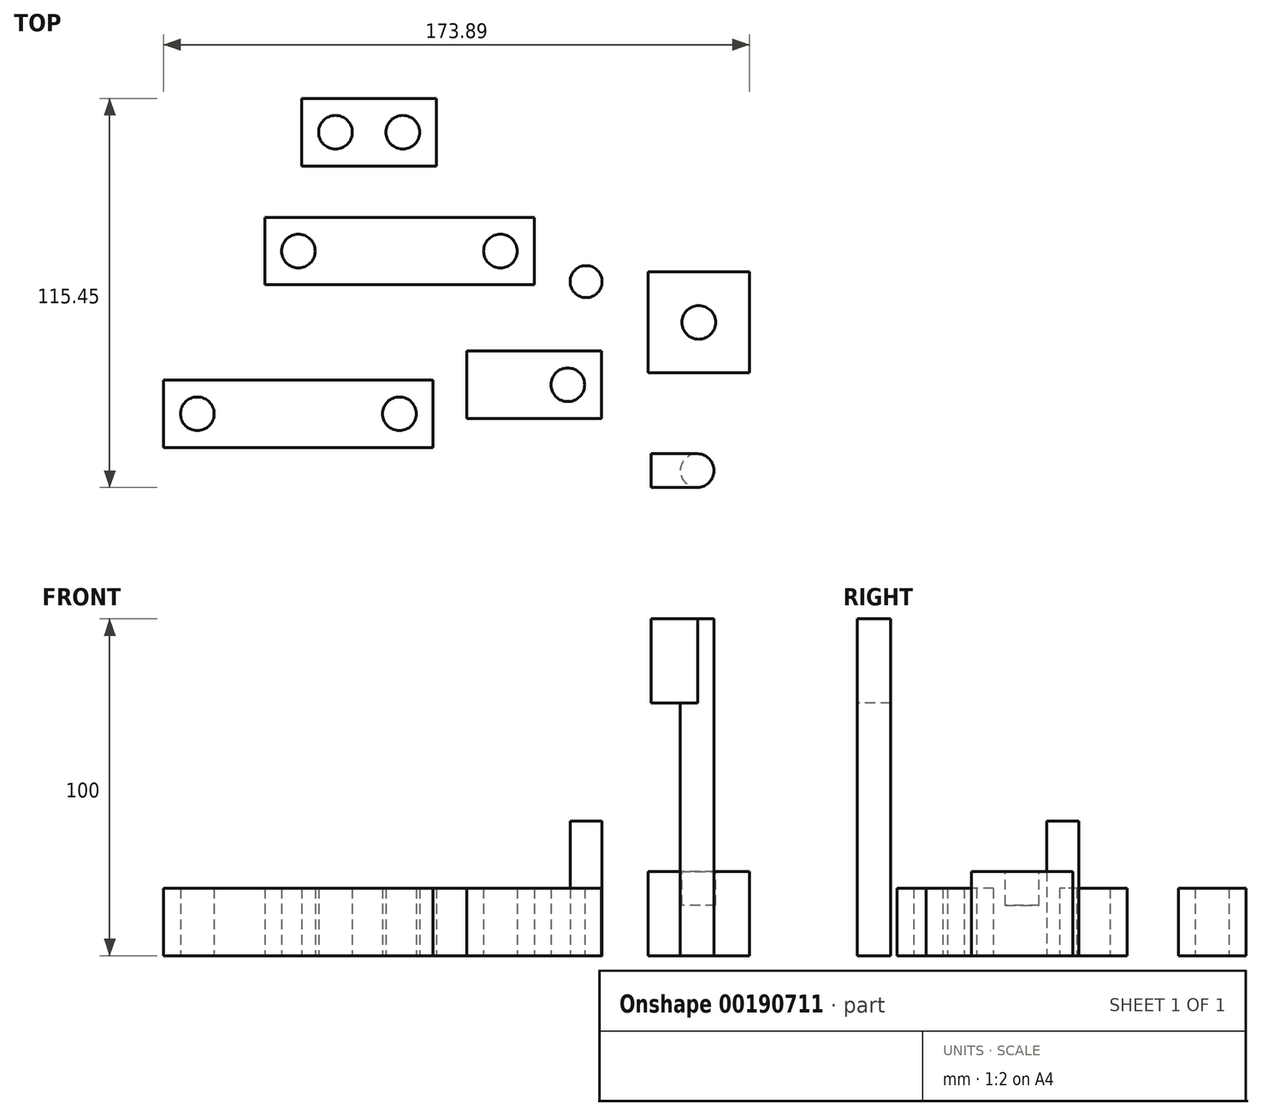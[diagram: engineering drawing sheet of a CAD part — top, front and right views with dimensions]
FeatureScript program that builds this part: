
annotation { "Feature Type Name" : "Feature", "Feature Type Description" : "" }
export const myFeature = defineFeature(function(context is Context, id is Id, definition is map)
    precondition{}
    {
        {
            var Q0;
            Q0=qCreatedBy(makeId("Top.planeOp"),FACE);
            var sketch = newSketch(context, id + "F0", { "sketchPlane" : qUnion([Q0])});
            skLineSegment(sketch, "E0.bottom", {"start": v(-30, 10) * mm, "end": v(10, 10) * mm});
            skLineSegment(sketch, "E0.top", {"start": v(-30, -10) * mm, "end": v(10, -10) * mm});
            skLineSegment(sketch, "E0.left", {"start": v(-30, 10) * mm, "end": v(-30, -10) * mm});
            skLineSegment(sketch, "E0.right", {"start": v(10, 10) * mm, "end": v(10, -10) * mm});
            skCircle(sketch, "E1", {"center": v(0, 0) * mm, "radius": 5 * mm});
            skSolve(sketch);
        }
        {
            var Q0;
            Q0=makeQuery(id+"F0.imprint","IMPRINT",FACE,{"disambiguationData":[TD([[makeQuery(id+"F0.imprint","IMPRINT",EDGE,{"derivedFrom":sQuery(id+"F0.wireOp",EDGE,"E0.bottom")}),-1.0]])]});
            extrude(context, id + "F1", {"entities" : qUnion([Q0]), "depth" : 20 * mm});
        }
        {
            var Q0;
            Q0=qCreatedBy(makeId("Top.planeOp"),FACE);
            var sketch = newSketch(context, id + "F2", { "sketchPlane" : qUnion([Q0])});
            skLineSegment(sketch, "E2.bottom", {"start": v(23.89, 33.53) * mm, "end": v(53.89, 33.53) * mm});
            skLineSegment(sketch, "E2.top", {"start": v(23.89, 3.53) * mm, "end": v(53.89, 3.53) * mm});
            skLineSegment(sketch, "E2.left", {"start": v(23.89, 33.53) * mm, "end": v(23.89, 3.53) * mm});
            skLineSegment(sketch, "E2.right", {"start": v(53.89, 33.53) * mm, "end": v(53.89, 3.53) * mm});
            skSolve(sketch);
        }
        {
            var Q0;
            Q0 = qSketchRegion(id + "F2", true);
            extrude(context, id + "F3", {"entities" : qUnion([Q0]), "depth" : 25 * mm});
        }
        {
            var Q0;
            Q0=makeQuery(id+"F3.opExtrude","CAP_FACE",FACE,{"disambiguationData":[OSD([sQuery(id+"F2.wireOp",EDGE,"E2.bottom"),sQuery(id+"F2.wireOp",EDGE,"E2.top"),sQuery(id+"F2.wireOp",EDGE,"E2.left"),sQuery(id+"F2.wireOp",EDGE,"E2.right"),sQuery(id+"F2.wireOp",EDGE,"gEPdtIbd-Eig8-yS6G-mVio-MUXTbyyWghyp")])],"isStart":false});
            var sketch = newSketch(context, id + "F4", { "sketchPlane" : qUnion([Q0])});
            skCircle(sketch, "E3", {"center": v(38.89, 18.53) * mm, "radius": 5 * mm});
            skPoint(sketch, "E3.first.point", {"position": v(43.88, 18.4) * mm});
            skPoint(sketch, "E3.second.point", {"position": v(39.58, 13.58) * mm});
            skPoint(sketch, "E3.third.point", {"position": v(34.82, 21.44) * mm});
            skSolve(sketch);
        }
        {
            var Q0;
            Q0 = qSketchRegion(id + "F4", true);
            extrude(context, id + "F5", {"entities" : qUnion([Q0]), "operationType" : NewBodyOperationType.REMOVE, "oppositeDirection" : true, "depth" : 10 * mm});
        }
        {
            var Q0;
            Q0=qCreatedBy(makeId("Top.planeOp"),FACE);
            var sketch = newSketch(context, id + "F6", { "sketchPlane" : qUnion([Q0])});
            skCircle(sketch, "E4", {"center": v(38.41, -25.48) * mm, "radius": 5 * mm});
            skSolve(sketch);
        }
        {
            var Q0;
            Q0 = qSketchRegion(id + "F6", true);
            extrude(context, id + "F7", {"entities" : qUnion([Q0]), "depth" : 100 * mm});
        }
        {
            var Q0;
            Q0=makeQuery(id+"F7.opExtrude","CAP_FACE",FACE,{"disambiguationData":[OSD([sQuery(id+"F6.wireOp",EDGE,"E4")])],"isStart":false});
            var sketch = newSketch(context, id + "F8", { "sketchPlane" : qUnion([Q0])});
            skLineSegment(sketch, "E5.bottom", {"start": v(38.56, -20.48) * mm, "end": v(24.68, -20.48) * mm});
            skLineSegment(sketch, "E5.top", {"start": v(38.56, -30.48) * mm, "end": v(24.68, -30.48) * mm});
            skLineSegment(sketch, "E5.left", {"start": v(38.56, -20.48) * mm, "end": v(38.56, -30.48) * mm});
            skLineSegment(sketch, "E5.right", {"start": v(24.68, -20.48) * mm, "end": v(24.68, -30.48) * mm});
            skSolve(sketch);
        }
        {
            var Q0;
            Q0 = qSketchRegion(id + "F8", true);
            extrude(context, id + "F9", {"entities" : qUnion([Q0]), "operationType" : NewBodyOperationType.ADD, "oppositeDirection" : true, "depth" : 25 * mm});
        }
        {
            var Q0;
            Q0=qCreatedBy(makeId("Top.planeOp"),FACE);
            var sketch = newSketch(context, id + "F10", { "sketchPlane" : qUnion([Q0])});
            skCircle(sketch, "E6", {"center": v(5.43, 30.62) * mm, "radius": 4.75 * mm});
            skSolve(sketch);
        }
        {
            var Q0;
            Q0=makeQuery(id+"F10.imprint","IMPRINT",FACE,{"disambiguationData":[TD([[makeQuery(id+"F10.imprint","IMPRINT",EDGE,{"derivedFrom":sQuery(id+"F10.wireOp",EDGE,"E6")}),1.0]])]});
            extrude(context, id + "F11", {"entities" : qUnion([Q0]), "depth" : 40 * mm});
        }
        {
            var Q0;
            Q0=qCreatedBy(makeId("Top.planeOp"),FACE);
            var sketch = newSketch(context, id + "F12", { "sketchPlane" : qUnion([Q0])});
            skLineSegment(sketch, "E7.bottom", {"start": v(-90, 49.7) * mm, "end": v(-10, 49.7) * mm});
            skLineSegment(sketch, "E7.top", {"start": v(-90, 29.7) * mm, "end": v(-10, 29.7) * mm});
            skLineSegment(sketch, "E7.left", {"start": v(-90, 49.7) * mm, "end": v(-90, 29.7) * mm});
            skLineSegment(sketch, "E7.right", {"start": v(-10, 49.7) * mm, "end": v(-10, 29.7) * mm});
            skCircle(sketch, "E8", {"center": v(-80, 39.7) * mm, "radius": 5 * mm});
            skCircle(sketch, "E9", {"center": v(-20, 39.7) * mm, "radius": 5 * mm});
            skSolve(sketch);
        }
        {
            var Q0;
            Q0 = qSketchRegion(id + "F12", true);
            extrude(context, id + "F13", {"entities" : qUnion([Q0]), "depth" : 20 * mm});
        }
        {
            var Q0;
            Q0=qCreatedBy(makeId("Top.planeOp"),FACE);
            var sketch = newSketch(context, id + "F14", { "sketchPlane" : qUnion([Q0])});
            skLineSegment(sketch, "E10.bottom", {"start": v(-78.98, 84.97) * mm, "end": v(-38.98, 84.97) * mm});
            skLineSegment(sketch, "E10.top", {"start": v(-78.98, 64.97) * mm, "end": v(-38.98, 64.97) * mm});
            skLineSegment(sketch, "E10.left", {"start": v(-78.98, 84.97) * mm, "end": v(-78.98, 64.97) * mm});
            skLineSegment(sketch, "E10.right", {"start": v(-38.98, 84.97) * mm, "end": v(-38.98, 64.97) * mm});
            skCircle(sketch, "E11", {"center": v(-68.98, 74.97) * mm, "radius": 5 * mm});
            skCircle(sketch, "E12", {"center": v(-48.98, 74.97) * mm, "radius": 5 * mm});
            skSolve(sketch);
        }
        {
            var Q0;
            Q0 = qSketchRegion(id + "F14", true);
            extrude(context, id + "F15", {"entities" : qUnion([Q0]), "depth" : 20 * mm});
        }
        {
            var Q0;
            Q0=qCreatedBy(makeId("Top.planeOp"),FACE);
            var sketch = newSketch(context, id + "F16", { "sketchPlane" : qUnion([Q0])});
            skLineSegment(sketch, "E13.bottom", {"start": v(-120, 1.4) * mm, "end": v(-40, 1.4) * mm});
            skLineSegment(sketch, "E13.top", {"start": v(-120, -18.6) * mm, "end": v(-40, -18.6) * mm});
            skLineSegment(sketch, "E13.left", {"start": v(-120, 1.4) * mm, "end": v(-120, -18.6) * mm});
            skLineSegment(sketch, "E13.right", {"start": v(-40, 1.4) * mm, "end": v(-40, -18.6) * mm});
            skCircle(sketch, "E14", {"center": v(-110, -8.6) * mm, "radius": 5 * mm});
            skPoint(sketch, "E14.centerSnap0", {"position": v(-120, -8.6) * mm});
            skCircle(sketch, "E15", {"center": v(-50, -8.6) * mm, "radius": 5 * mm});
            skSolve(sketch);
        }
        {
            var Q0;
            Q0 = qSketchRegion(id + "F16", true);
            extrude(context, id + "F17", {"entities" : qUnion([Q0]), "depth" : 20 * mm});
        }
    });
